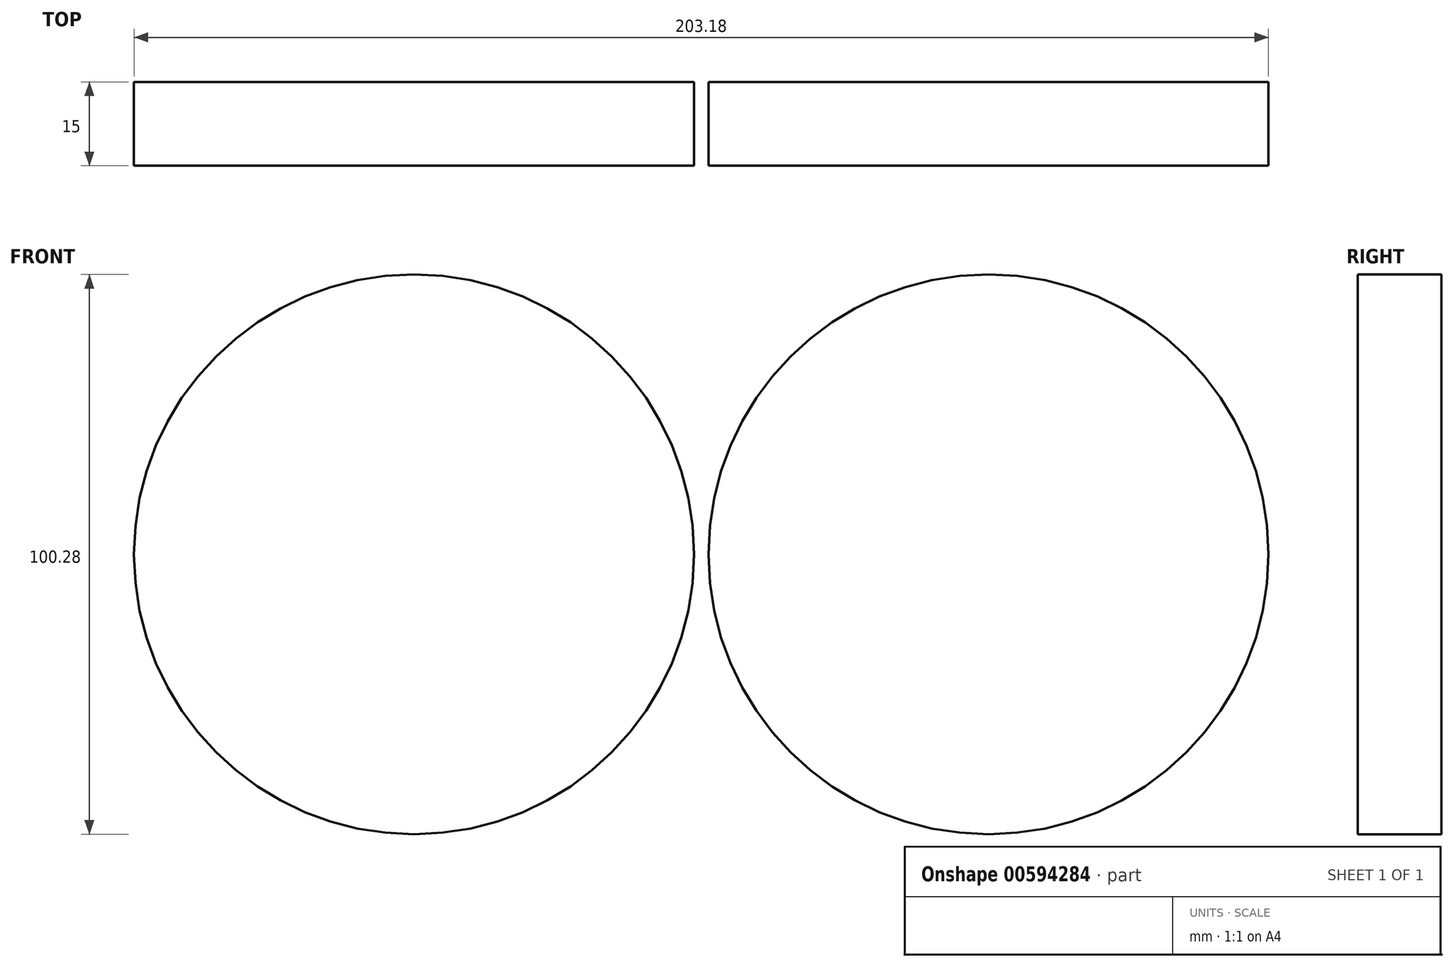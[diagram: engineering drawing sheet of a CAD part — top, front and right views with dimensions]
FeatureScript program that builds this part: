
annotation { "Feature Type Name" : "Feature", "Feature Type Description" : "" }
export const myFeature = defineFeature(function(context is Context, id is Id, definition is map)
    precondition{}
    {
        {
            var Q0;
            Q0=qCreatedBy(makeId("Front.planeOp"),FACE);
            var sketch = newSketch(context, id + "F0", { "sketchPlane" : qUnion([Q0])});
            skArc(sketch, "E0", {"start": v(55.6, 0) * mm, "mid": v(0, 55.6) * mm, "end": v(-55.6, 0) * mm});
            skLineSegment(sketch, "E1", {"start": v(0, 0) * mm, "end": v(55.6, 0) * mm});
            skLineSegment(sketch, "E2", {"start": v(0, 55.6) * mm, "end": v(0, -65.33) * mm});
            skSolve(sketch);
        }
        {
            var Q0;
            Q0 = qSketchRegion(id + "F0", true);
            var Q1;
            Q1=sQuery(id+"F0.wireOp",EDGE,"E0");
            var Q2;
            Q2=sQuery(id+"F0.wireOp",EDGE,"E1");
            revolve(context, id + "F1", {"bodyType" : ToolBodyType.SURFACE, "entities" : qUnion([Q0]), "surfaceEntities" : qUnion([Q1]), "axis" : qUnion([Q2]), "revolveType" : RevolveType.FULL});
        }
        {
            var Q0;
            Q0=qCreatedBy(makeId("Front.planeOp"),FACE);
            var sketch = newSketch(context, id + "F2", { "sketchPlane" : qUnion([Q0])});
            skArc(sketch, "E3", {"start": v(-30.64, 50.09) * mm, "mid": v(-46.5, 66.2) * mm, "end": v(-62.57, 50.32) * mm});
            skLineSegment(sketch, "E4", {"start": v(-62.57, 50.32) * mm, "end": v(-30.64, 50.09) * mm});
            skArc(sketch, "E5.MirrorCS", {"start": v(30.64, 50.09) * mm, "mid": v(46.5, 66.2) * mm, "end": v(62.57, 50.32) * mm});
            skLineSegment(sketch, "E6.MirrorCS", {"start": v(62.57, 50.32) * mm, "end": v(30.64, 50.09) * mm});
            skSolve(sketch);
        }
        {
            var Q0;
            Q0=sQuery(id+"F2.wireOp",EDGE,"E3");
            var Q1;
            Q1=sQuery(id+"F2.wireOp",EDGE,"E4");
            revolve(context, id + "F3", {"bodyType" : ToolBodyType.SURFACE, "surfaceEntities" : qUnion([Q0]), "axis" : qUnion([Q1]), "revolveType" : RevolveType.FULL});
        }
        {
            var Q0;
            Q0=makeQuery(id+"F3.opRevolve","SWEPT_BODY",BODY,{"disambiguationData":[OSD([sQuery(id+"F2.wireOp",EDGE,"E3")])]});
            transform(context, id + "F4", {"entities" : qUnion([Q0]), "transformType" : TransformType.TRANSLATION_3D, "dx" : 12.7 * mm, "dy" : -25.4 * mm, "dz" : -12.7 * mm, "makeCopy" : false});
        }
        {
            var Q0;
            Q0=sQuery(id+"F2.wireOp",EDGE,"E5.MirrorCS");
            var Q1;
            Q1=sQuery(id+"F2.wireOp",EDGE,"E6.MirrorCS");
            revolve(context, id + "F5", {"bodyType" : ToolBodyType.SURFACE, "surfaceEntities" : qUnion([Q0]), "axis" : qUnion([Q1]), "revolveType" : RevolveType.FULL});
        }
        {
            var Q0;
            Q0=makeQuery(id+"F5.opRevolve","SWEPT_BODY",BODY,{"disambiguationData":[OSD([sQuery(id+"F2.wireOp",EDGE,"E5.MirrorCS")])]});
            transform(context, id + "F6", {"entities" : qUnion([Q0]), "transformType" : TransformType.TRANSLATION_3D, "dx" : -12.7 * mm, "dy" : -25.4 * mm, "dz" : -12.7 * mm, "makeCopy" : false});
        }
        {
            var Q0;
            Q0=qCreatedBy(makeId("Front.planeOp"),FACE);
            var sketch = newSketch(context, id + "F7", { "sketchPlane" : qUnion([Q0])});
            skLineSegment(sketch, "E7.bottom", {"start": v(0.35, 120.14) * mm, "end": v(120.35, 120.14) * mm});
            skLineSegment(sketch, "E7.top", {"start": v(0.35, 0.14) * mm, "end": v(120.35, 0.14) * mm});
            skLineSegment(sketch, "E7.left", {"start": v(0.35, 120.14) * mm, "end": v(0.35, 0) * mm});
            skLineSegment(sketch, "E7.right", {"start": v(120.35, 120.14) * mm, "end": v(120.35, 0.14) * mm});
            skLineSegment(sketch, "E8.MirrorCS", {"start": v(0.35, 120.14) * mm, "end": v(-119.65, 120.14) * mm});
            skLineSegment(sketch, "E9.MirrorCS", {"start": v(-119.65, 120.14) * mm, "end": v(-119.65, 0.14) * mm});
            skLineSegment(sketch, "E10.MirrorCS", {"start": v(0.35, 0.14) * mm, "end": v(-119.65, 0.14) * mm});
            skSolve(sketch);
        }
        {
            var Q0;
            Q0 = qSketchRegion(id + "F7", true);
            extrude(context, id + "F8", {"entities" : qUnion([Q0]), "depth" : 15 * mm, "offsetDistance" : 25.4 * mm});
        }
        {
            var Q0;
            Q0=makeQuery(id+"F8.opExtrude","CAP_FACE",FACE,{"disambiguationData":[OSD([sQuery(id+"F7.wireOp",EDGE,"E7.bottom"),sQuery(id+"F7.wireOp",EDGE,"E7.top"),sQuery(id+"F7.wireOp",EDGE,"E7.left"),sQuery(id+"F7.wireOp",EDGE,"E7.right")])],"isStart":false});
            var sketch = newSketch(context, id + "F9", { "sketchPlane" : qUnion([Q0])});
            skCircle(sketch, "E11", {"center": v(51.8, 63.9) * mm, "radius": 50.14 * mm});
            skLineSegment(sketch, "E12", {"start": v(0.35, -75.4) * mm, "end": v(0.35, 126.07) * mm});
            skPoint(sketch, "E12.startSnap0", {"position": v(0.35, 120.14) * mm});
            skCircle(sketch, "E13.MirrorC", {"center": v(-51.1, 63.9) * mm, "radius": 50.14 * mm});
            skSolve(sketch);
        }
        {
            var Q0;
            Q0 = qSketchRegion(id + "F9", true);
            extrude(context, id + "F10", {"entities" : qUnion([Q0]), "operationType" : NewBodyOperationType.INTERSECT, "oppositeDirection" : true, "depth" : 25 * mm, "offsetDistance" : 25 * mm});
        }
    });
